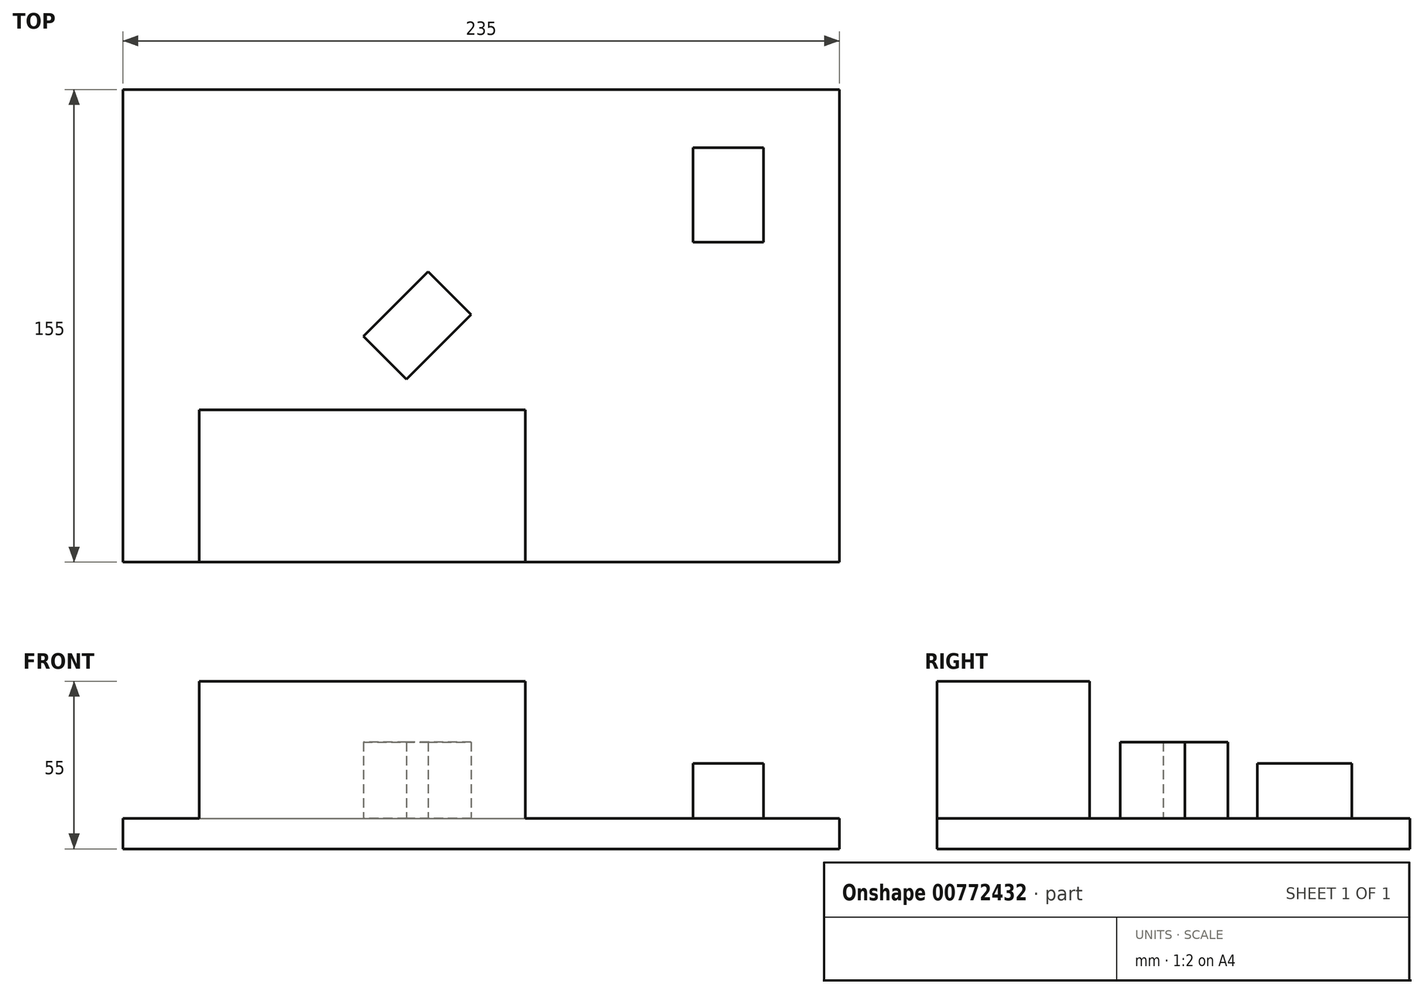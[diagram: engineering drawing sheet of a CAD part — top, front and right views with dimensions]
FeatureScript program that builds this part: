
annotation { "Feature Type Name" : "Feature", "Feature Type Description" : "" }
export const myFeature = defineFeature(function(context is Context, id is Id, definition is map)
    precondition{}
    {
        {
            var Q0;
            Q0=qCreatedBy(makeId("Top.planeOp"),FACE);
            var sketch = newSketch(context, id + "F0", { "sketchPlane" : qUnion([Q0])});
            skLineSegment(sketch, "E0.bottom", {"start": v(0, 0) * mm, "end": v(235, 0) * mm});
            skLineSegment(sketch, "E0.top", {"start": v(0, 155) * mm, "end": v(235, 155) * mm});
            skLineSegment(sketch, "E0.left", {"start": v(0, 0) * mm, "end": v(0, 155) * mm});
            skLineSegment(sketch, "E0.right", {"start": v(235, 0) * mm, "end": v(235, 155) * mm});
            skSolve(sketch);
        }
        {
            var Q0;
            Q0=makeQuery(id+"F0.imprint","IMPRINT",FACE,{"disambiguationData":[TD([[makeQuery(id+"F0.imprint","IMPRINT",EDGE,{"derivedFrom":sQuery(id+"F0.wireOp",EDGE,"E0.bottom")}),1.0]])]});
            extrude(context, id + "F1", {"entities" : qUnion([Q0]), "depth" : 10 * mm, "offsetDistance" : 25 * mm});
        }
        {
            var Q0;
            Q0=makeQuery(id+"F1.opExtrude","CAP_FACE",FACE,{"disambiguationData":[OSD([sQuery(id+"F0.wireOp",EDGE,"E0.bottom"),sQuery(id+"F0.wireOp",EDGE,"E0.top"),sQuery(id+"F0.wireOp",EDGE,"E0.left"),sQuery(id+"F0.wireOp",EDGE,"E0.right")])],"isStart":false});
            var sketch = newSketch(context, id + "F2", { "sketchPlane" : qUnion([Q0])});
            skLineSegment(sketch, "E1.bottom", {"start": v(25, 0) * mm, "end": v(132, 0) * mm});
            skLineSegment(sketch, "E1.top", {"start": v(25, 50) * mm, "end": v(132, 50) * mm});
            skLineSegment(sketch, "E1.left", {"start": v(25, 0) * mm, "end": v(25, 50) * mm});
            skLineSegment(sketch, "E1.right", {"start": v(132, 0) * mm, "end": v(132, 50) * mm});
            skSolve(sketch);
        }
        {
            var Q0;
            Q0=makeQuery(id+"F2.imprint","IMPRINT",FACE,{"disambiguationData":[TD([[makeQuery(id+"F2.imprint","IMPRINT",EDGE,{"derivedFrom":sQuery(id+"F2.wireOp",EDGE,"E1.bottom")}),1.0]])]});
            extrude(context, id + "F3", {"entities" : qUnion([Q0]), "operationType" : NewBodyOperationType.ADD, "depth" : 45 * mm, "offsetDistance" : 25 * mm});
        }
        {
            var Q0;
            Q0=makeQuery(id+"F1.opExtrude","CAP_FACE",FACE,{"disambiguationData":[OSD([sQuery(id+"F0.wireOp",EDGE,"E0.bottom"),sQuery(id+"F0.wireOp",EDGE,"E0.top"),sQuery(id+"F0.wireOp",EDGE,"E0.left"),sQuery(id+"F0.wireOp",EDGE,"E0.right")])],"isStart":false});
            var sketch = newSketch(context, id + "F4", { "sketchPlane" : qUnion([Q0])});
            skLineSegment(sketch, "E2.bottom", {"start": v(210, 136) * mm, "end": v(187, 136) * mm});
            skLineSegment(sketch, "E2.top", {"start": v(210, 105) * mm, "end": v(187, 105) * mm});
            skLineSegment(sketch, "E2.left", {"start": v(210, 136) * mm, "end": v(210, 105) * mm});
            skLineSegment(sketch, "E2.right", {"start": v(187, 136) * mm, "end": v(187, 105) * mm});
            skSolve(sketch);
        }
        {
            var Q0;
            Q0=makeQuery(id+"F4.imprint","IMPRINT",FACE,{"disambiguationData":[TD([[makeQuery(id+"F4.imprint","IMPRINT",EDGE,{"derivedFrom":sQuery(id+"F4.wireOp",EDGE,"E2.bottom")}),1.0]])]});
            extrude(context, id + "F5", {"entities" : qUnion([Q0]), "operationType" : NewBodyOperationType.ADD, "depth" : 18 * mm, "offsetDistance" : 25 * mm});
        }
        {
            var Q0;
            Q0=makeQuery(id+"F1.opExtrude","CAP_FACE",FACE,{"disambiguationData":[OSD([sQuery(id+"F0.wireOp",EDGE,"E0.bottom"),sQuery(id+"F0.wireOp",EDGE,"E0.top"),sQuery(id+"F0.wireOp",EDGE,"E0.left"),sQuery(id+"F0.wireOp",EDGE,"E0.right")])],"isStart":false});
            var sketch = newSketch(context, id + "F6", { "sketchPlane" : qUnion([Q0])});
            skLineSegment(sketch, "E3", {"start": v(78.86, 74.14) * mm, "end": v(100.07, 95.36) * mm});
            skLineSegment(sketch, "E4", {"start": v(100.07, 95.36) * mm, "end": v(114.21, 81.21) * mm});
            skLineSegment(sketch, "E5", {"start": v(114.21, 81.21) * mm, "end": v(93, 60) * mm});
            skLineSegment(sketch, "E6", {"start": v(93, 60) * mm, "end": v(78.86, 74.14) * mm});
            skSolve(sketch);
        }
        {
            var Q0;
            Q0=makeQuery(id+"F6.imprint","IMPRINT",FACE,{"disambiguationData":[TD([[makeQuery(id+"F6.imprint","IMPRINT",EDGE,{"derivedFrom":sQuery(id+"F6.wireOp",EDGE,"E3")}),-1.0]])]});
            extrude(context, id + "F7", {"entities" : qUnion([Q0]), "operationType" : NewBodyOperationType.ADD, "depth" : 25 * mm, "offsetDistance" : 25 * mm});
        }
    });
